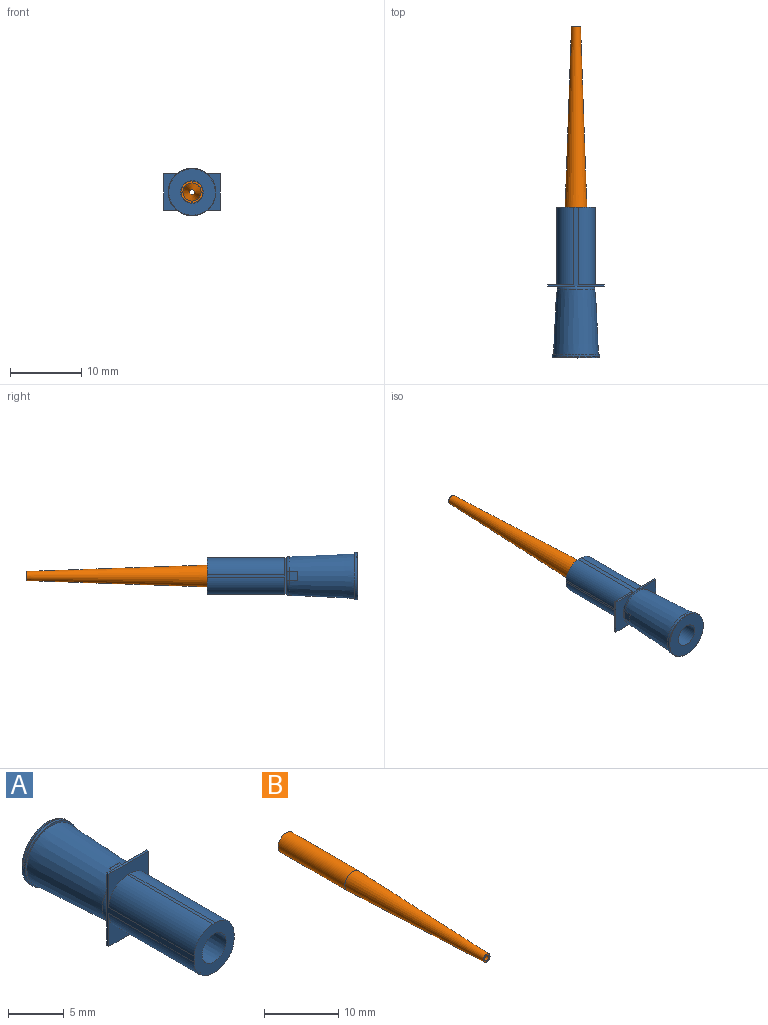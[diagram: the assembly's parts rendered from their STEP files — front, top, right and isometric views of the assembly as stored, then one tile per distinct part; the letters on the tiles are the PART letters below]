
ASSEMBLY  parts=2 mates=1
PART A: 38 faces, bbox 6.8x21.3x8 mm
  f0: plane 11.11x0.01mm, normal (0,0,1), area 0.1mm2, adj f1,f4,f25,f32
  f1: cylinder r=2.54mm len=11.11mm, axis (0,1,0), area 0.2mm2, adj f0,f4,f9,f32
  f2: cone r=1.91mm half-angle=1deg, axis (0,1,0), area 131.4mm2, adj f4,f15,f33
  f3: plane 10.86x0.3mm, normal (0,0,-1), area 3.2mm2, adj f4,f26,f36,f37
  f4: plane 5.43x5.08mm, normal (0,-1,0), area 15.3mm2, adj f0,f1,f2,f3,f24,f28,f29,f32
  f5: cylinder r=3.33mm len=6.67mm, axis (0,1,0), area 7.4mm2, adj f6,f8,f11,f12,f13,f14
  f6: cylinder r=3.33mm len=6.67mm, axis (0,1,0), area 0.8mm2, adj f5,f8,f13
  f7: cone r=3.17mm half-angle=2.7deg, axis (0,1,0), area 166.3mm2, adj f9,f10,f11,f17,f18,f20,f21
  f8: plane 6.74x6.67mm, normal (0,1,0), area 26.7mm2, adj f5,f6,f13,f14,f16
  f9: torus R=2.12mm, axis (0,-1,0), area 3.2mm2, adj f1,f7,f19,f22,f23,f25
  f10: torus R=2.12mm, axis (0,-1,0), area 3.2mm2, adj f7,f19,f22,f23,f25
  f11: plane 6.67x6.67mm, normal (0,-1,0), area 3.7mm2, adj f5,f7
  f12: plane 0.09x0.08mm, normal (0,0,1), area 0mm2, adj f5,f13,f14
  f13: bspline ~7.77x6.72mm, area 1.7mm2, adj f5,f6,f8,f12,f14
  f14: bspline ~7.77x6.72mm, area 2.1mm2, adj f5,f8,f12,f13
  f15: plane 3.51x3.51mm, normal (0,-1,0), area 1.8mm2, adj f2,f16
  f16: cylinder r=1.59mm len=8.47mm, axis (0,1,0), area 84.5mm2, adj f8,f15
  f17: plane 1.27x0.07mm, normal (0,-1,0), area 0.1mm2, adj f7,f18
  f18: extruded ~1.27x1.19mm, area 1.5mm2, adj f7,f17,f19
  f19: extruded ~1.27x0.4mm, area 0.6mm2, adj f9,f10,f18,f25
  f20: plane 1.27x0.07mm, normal (0,-1,0), area 0.1mm2, adj f7,f21
  f21: plane 1.27x1.19mm, normal (0,-0.05,1), area 1.5mm2, adj f7,f20,f22
  f22: extruded ~1.27x0.4mm, area 0.6mm2, adj f9,f10,f21,f23
  f23: plane 5.08x3.98mm, normal (0,1,0), area 10.2mm2, adj f9,f10,f22,f28,f29,f31
  f24: plane 10.86x0.3mm, normal (0,0,1), area 3.2mm2, adj f4,f30,f34,f35
  f25: plane 5.08x3.98mm, normal (0,1,0), area 10.2mm2, adj f0,f9,f10,f19,f27,f28,f29,f32
  f26: plane 5.08x3.66mm, normal (0,-1,0), area 8.9mm2, adj f3,f27,f28,f29,f36,f37
  f27: plane 5.08x0.25mm, normal (0,0,-1), area 1.3mm2, adj f25,f26,f28,f29
  f28: plane 11.11x7.97mm, normal (1,0,0), area 9mm2, adj f4,f23,f25,f26,f27,f30,f31,f34
  f29: plane 11.11x7.97mm, normal (-1,0,0), area 9mm2, adj f4,f23,f25,f26,f27,f30,f31,f35
  f30: plane 5.08x3.66mm, normal (0,-1,0), area 8.9mm2, adj f24,f28,f29,f31,f34,f35
  f31: plane 5.08x0.25mm, normal (0,0,1), area 1.3mm2, adj f23,f28,f29,f30
  f32: plane 11.11x0.01mm, normal (1,0,0), area 0.1mm2, adj f0,f1,f4,f25
  f33: plane 0.13x0.07mm, normal (-1,0,0), area 0mm2, adj f2
  f34: cylinder r=2.39mm len=10.86mm, axis (0,-1,0), area 40.8mm2, adj f4,f24,f28,f30
  f35: cylinder r=2.39mm len=10.86mm, axis (0,1,0), area 40.8mm2, adj f4,f24,f29,f30
  f36: cylinder r=2.39mm len=10.86mm, axis (0,-1,0), area 40.8mm2, adj f3,f4,f26,f29
  f37: cylinder r=2.39mm len=10.86mm, axis (0,1,0), area 40.8mm2, adj f3,f4,f26,f28
PART B: 7 faces, bbox 3.1x38.1x3.1 mm
  f0: cylinder r=1.27mm len=12.69mm, axis (0,-1,0), area 101.3mm2, adj f1,f5
  f1: plane 3.07x3.07mm, normal (0,1,0), area 2.3mm2, adj f0,f2
  f2: cylinder r=1.54mm len=12.7mm, axis (0,-1,0), area 122.5mm2, adj f1,f3
  f3: plane 3.07x3.07mm, normal (0,-1,0), area 0.1mm2, adj f2,f6
  f4: plane 1.27x1.27mm, normal (0,-1,0), area 0.8mm2, adj f5,f6
  f5: cone r=1.27mm half-angle=2deg, axis (0,1,0), area 131.9mm2, adj f0,f4
  f6: cone r=1.52mm half-angle=2deg, axis (0,1,0), area 172.4mm2, adj f3,f4
PLACE A rot(axis=(-0.71,0,-0.71),180deg) t=(0,-25.4,0)mm
PLACE B rot(axis=(-1,0,0),180deg) t=(0,-25.4,0)mm
MATE fastened A.f2 <-> B.f6  axis (0,1,0) through (0,-12.7,0)mm
